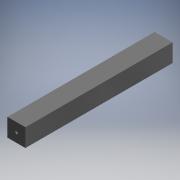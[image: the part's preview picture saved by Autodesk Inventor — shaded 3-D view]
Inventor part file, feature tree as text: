
AUTODESK INVENTOR PART (.ipt)
format: ipt  version: 2019 (Build 230136000, 136)  size: 94,720 bytes
history: native  units: mm (DEFAULTED — no unit token found)
features: extrude x2, sketch x2
ambient origin geometry x8: Origin, YZ Plane, XZ Plane, XY Plane, X Axis, Y Axis, Z Axis, Center Point
bodies: Solid1 (feature_tree)
feature tree (4):
  extrude  "Extrusion1"  Depth=31.75mm
  extrude  "Extrusion2"  Depth=31.75mm
  sketch  "Sketch1"  dims[d0=31.75mm d1=31.75mm]
  sketch  "Sketch2"  dims[d2=260.35mm d3=0.0mm d4=5.08mm d5=31.75mm d6=15.875mm d7=15.875mm d8=269.24mm d9=0.0mm]
